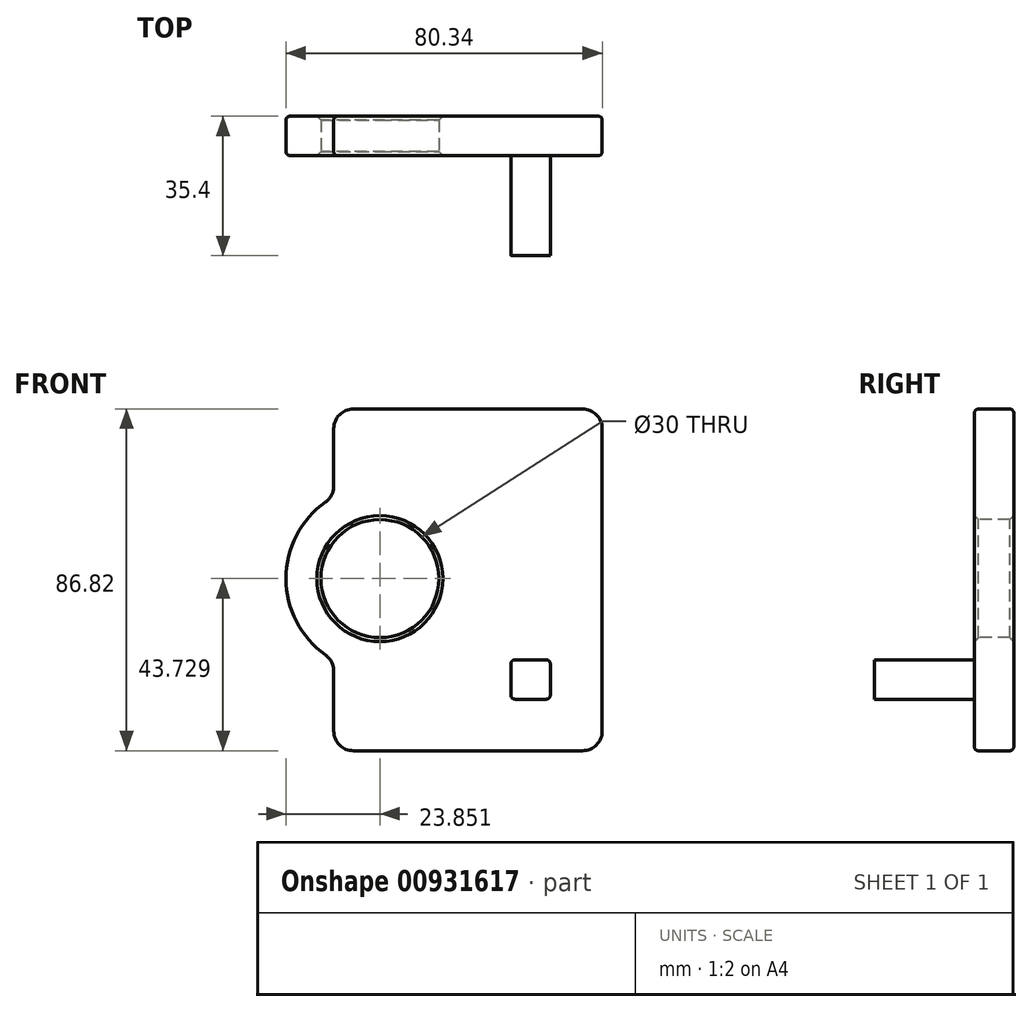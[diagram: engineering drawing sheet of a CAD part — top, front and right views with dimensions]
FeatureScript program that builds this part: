
annotation { "Feature Type Name" : "Feature", "Feature Type Description" : "" }
export const myFeature = defineFeature(function(context is Context, id is Id, definition is map)
    precondition{}
    {
        {
            var Q0;
            Q0=qCreatedBy(makeId("Front.planeOp"),FACE);
            var sketch = newSketch(context, id + "F0", { "sketchPlane" : qUnion([Q0])});
            skLineSegment(sketch, "E0.bottom", {"start": v(-35.93, 50.36) * mm, "end": v(32.27, 50.36) * mm});
            skLineSegment(sketch, "E0.top", {"start": v(-35.93, -36.46) * mm, "end": v(32.27, -36.46) * mm});
            skLineSegment(sketch, "E0.left", {"start": v(-35.93, 50.36) * mm, "end": v(-35.93, 28.04) * mm});
            skLineSegment(sketch, "E0.right", {"start": v(32.27, 50.36) * mm, "end": v(32.27, -36.46) * mm});
            skArc(sketch, "E1", {"start": v(-35.93, 28.04) * mm, "mid": v(-48.07, 7.27) * mm, "end": v(-35.93, -13.5) * mm});
            skLineSegment(sketch, "E2.trimOffspring", {"start": v(-35.93, -13.5) * mm, "end": v(-35.93, -36.46) * mm});
            skCircle(sketch, "E3", {"center": v(-24.22, 7.27) * mm, "radius": 15 * mm});
            skSolve(sketch);
        }
        {
            var Q0;
            Q0 = qSketchRegion(id + "F0", true);
            extrude(context, id + "F1", {"entities" : qUnion([Q0]), "oppositeDirection" : true, "depth" : 10 * mm, "offsetDistance" : 25.4 * mm});
        }
        {
            var Q0;
            Q0=makeQuery(id+"F1.opExtrude","SWEPT_EDGE",EDGE,{"disambiguationData":[OSD([sQuery(id+"F0.wireOp",EDGE,"E0.left"),sQuery(id+"F0.wireOp",EDGE,"E1")])]});
            var Q1;
            Q1=makeQuery(id+"F1.opExtrude","SWEPT_EDGE",EDGE,{"disambiguationData":[OSD([sQuery(id+"F0.wireOp",EDGE,"E1"),sQuery(id+"F0.wireOp",EDGE,"E2.trimOffspring")])]});
            var Q2;
            Q2=makeQuery(id+"F1.opExtrude","SWEPT_EDGE",EDGE,{"disambiguationData":[OSD([sQuery(id+"F0.wireOp",EDGE,"E0.bottom"),sQuery(id+"F0.wireOp",EDGE,"E0.left")])]});
            var Q3;
            Q3=makeQuery(id+"F1.opExtrude","SWEPT_EDGE",EDGE,{"disambiguationData":[OSD([sQuery(id+"F0.wireOp",EDGE,"E0.top"),sQuery(id+"F0.wireOp",EDGE,"E2.trimOffspring")])]});
            var Q4;
            Q4=makeQuery(id+"F1.opExtrude","SWEPT_EDGE",EDGE,{"disambiguationData":[OSD([sQuery(id+"F0.wireOp",EDGE,"E0.bottom"),sQuery(id+"F0.wireOp",EDGE,"E0.right")])]});
            var Q5;
            Q5=makeQuery(id+"F1.opExtrude","SWEPT_EDGE",EDGE,{"disambiguationData":[OSD([sQuery(id+"F0.wireOp",EDGE,"E0.top"),sQuery(id+"F0.wireOp",EDGE,"E0.right")])]});
            fillet(context, id + "F2", {"entities" : qUnion([Q0, Q1, Q2, Q3, Q4, Q5]), "radius" : 5 * mm, "tangentPropagation" : true, "allowEdgeOverflow" : false});
        }
        {
            var Q0;
            Q0=makeQuery(id+"F1.opExtrude","CAP_EDGE",EDGE,{"disambiguationData":[OSD([sQuery(id+"F0.wireOp",EDGE,"E3")])],"isStart":false});
            var Q1;
            Q1=makeQuery(id+"F1.opExtrude","CAP_EDGE",EDGE,{"disambiguationData":[OSD([sQuery(id+"F0.wireOp",EDGE,"E3")])],"isStart":true});
            chamfer(context, id + "F3", {"entities" : qUnion([Q0, Q1]), "width" : 1 * mm, "tangentPropagation" : true});
        }
        {
            var Q0;
            Q0=makeQuery(id+"F1.opExtrude","CAP_EDGE",EDGE,{"disambiguationData":[OSD([sQuery(id+"F0.wireOp",EDGE,"E0.bottom")])],"isStart":false});
            var Q1;
            Q1=makeQuery(id+"F1.opExtrude","CAP_EDGE",EDGE,{"disambiguationData":[OSD([sQuery(id+"F0.wireOp",EDGE,"E0.right")])],"isStart":true});
            fillet(context, id + "F4", {"entities" : qUnion([Q0, Q1]), "radius" : 1 * mm, "tangentPropagation" : true, "allowEdgeOverflow" : false});
        }
        {
            var Q0;
            Q0=qCreatedBy(makeId("Front.planeOp"),FACE);
            var sketch = newSketch(context, id + "F5", { "sketchPlane" : qUnion([Q0])});
            skLineSegment(sketch, "E4.bottom", {"start": v(9.07, -13.36) * mm, "end": v(19.07, -13.36) * mm});
            skLineSegment(sketch, "E4.top", {"start": v(9.07, -23.36) * mm, "end": v(19.07, -23.36) * mm});
            skLineSegment(sketch, "E4.left", {"start": v(9.07, -13.36) * mm, "end": v(9.07, -23.36) * mm});
            skLineSegment(sketch, "E4.right", {"start": v(19.07, -13.36) * mm, "end": v(19.07, -23.36) * mm});
            skSolve(sketch);
        }
        {
            var Q0;
            Q0=makeQuery(id+"F5.imprint","IMPRINT",FACE,{"disambiguationData":[TD([[makeQuery(id+"F5.imprint","IMPRINT",EDGE,{"derivedFrom":sQuery(id+"F5.wireOp",EDGE,"E4.bottom")}),-1.0]])]});
            extrude(context, id + "F6", {"entities" : qUnion([Q0]), "operationType" : NewBodyOperationType.ADD, "depth" : 25.4 * mm, "offsetDistance" : 25.4 * mm});
        }
        {
            var Q0;
            Q0=makeQuery(id+"F6.opExtrude","SWEPT_EDGE",EDGE,{"disambiguationData":[OSD([sQuery(id+"F5.wireOp",EDGE,"E4.top"),sQuery(id+"F5.wireOp",EDGE,"E4.right")])]});
            var Q1;
            Q1=makeQuery(id+"F6.opExtrude","SWEPT_EDGE",EDGE,{"disambiguationData":[OSD([sQuery(id+"F5.wireOp",EDGE,"E4.top"),sQuery(id+"F5.wireOp",EDGE,"E4.left")])]});
            var Q2;
            Q2=makeQuery(id+"F6.opExtrude","SWEPT_EDGE",EDGE,{"disambiguationData":[OSD([sQuery(id+"F5.wireOp",EDGE,"E4.bottom"),sQuery(id+"F5.wireOp",EDGE,"E4.left")])]});
            var Q3;
            Q3=makeQuery(id+"F6.opExtrude","SWEPT_EDGE",EDGE,{"disambiguationData":[OSD([sQuery(id+"F5.wireOp",EDGE,"E4.bottom"),sQuery(id+"F5.wireOp",EDGE,"E4.right")])]});
            fillet(context, id + "F7", {"entities" : qUnion([Q0, Q1, Q2, Q3]), "radius" : 1 * mm, "tangentPropagation" : true, "allowEdgeOverflow" : false});
        }
    });
